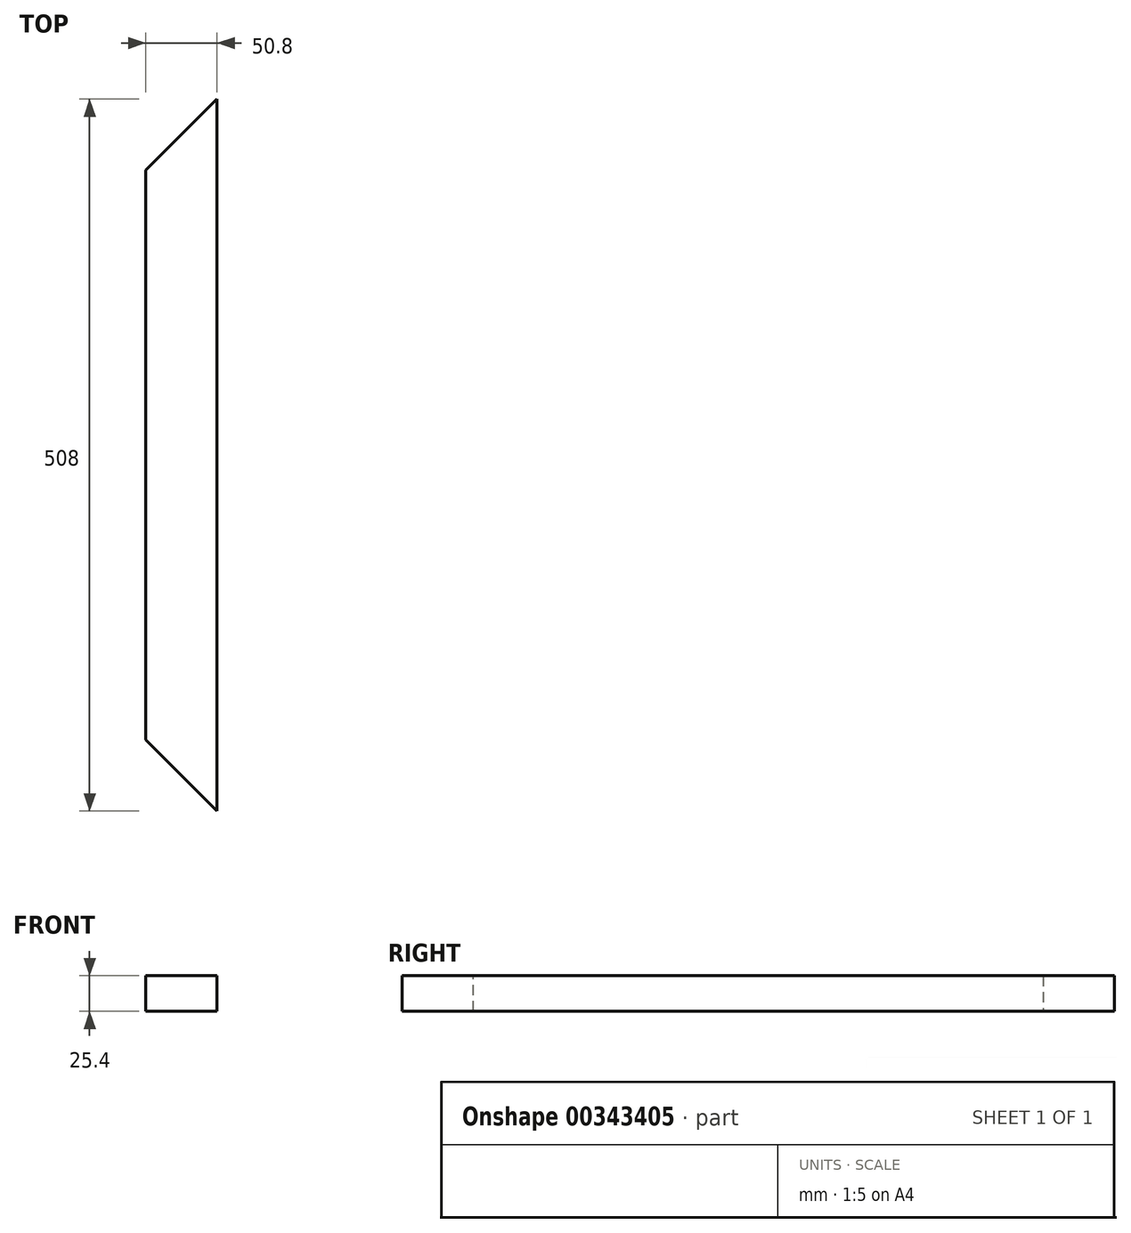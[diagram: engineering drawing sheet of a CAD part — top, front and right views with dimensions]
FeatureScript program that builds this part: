
annotation { "Feature Type Name" : "Feature", "Feature Type Description" : "" }
export const myFeature = defineFeature(function(context is Context, id is Id, definition is map)
    precondition{}
    {
        {
            var Q0;
            Q0=qCreatedBy(makeId("Front.planeOp"),FACE);
            var sketch = newSketch(context, id + "F0", { "sketchPlane" : qUnion([Q0])});
            skLineSegment(sketch, "E0.bottom", {"start": v(-32.55, 24) * mm, "end": v(18.25, 24) * mm});
            skLineSegment(sketch, "E0.top", {"start": v(-32.55, -1.4) * mm, "end": v(18.25, -1.4) * mm});
            skLineSegment(sketch, "E0.left", {"start": v(-32.55, 24) * mm, "end": v(-32.55, -1.4) * mm});
            skLineSegment(sketch, "E0.right", {"start": v(18.25, 24) * mm, "end": v(18.25, -1.4) * mm});
            skPoint(sketch, "E0.middle", {"position": v(-7.15, 11.3) * mm});
            skSolve(sketch);
        }
        {
            var Q0;
            Q0=makeQuery(id+"F0.imprint","IMPRINT",FACE,{"disambiguationData":[TD([[makeQuery(id+"F0.imprint","IMPRINT",EDGE,{"derivedFrom":sQuery(id+"F0.wireOp",EDGE,"E0.bottom")}),-1.0]])]});
            extrude(context, id + "F1", {"entities" : qUnion([Q0]), "depth" : 508 * mm});
        }
        {
            var Q0;
            Q0=makeQuery(id+"F1.opExtrude","CAP_EDGE",EDGE,{"disambiguationData":[OSD([sQuery(id+"F0.wireOp",EDGE,"E0.left")])],"isStart":false});
            chamfer(context, id + "F2", {"entities" : qUnion([Q0]), "width" : 50.8 * mm, "tangentPropagation" : true});
        }
        {
            var Q0;
            Q0=makeQuery(id+"F1.opExtrude","CAP_EDGE",EDGE,{"disambiguationData":[OSD([sQuery(id+"F0.wireOp",EDGE,"E0.left")])],"isStart":true});
            chamfer(context, id + "F3", {"entities" : qUnion([Q0]), "width" : 50.8 * mm, "tangentPropagation" : true});
        }
    });
